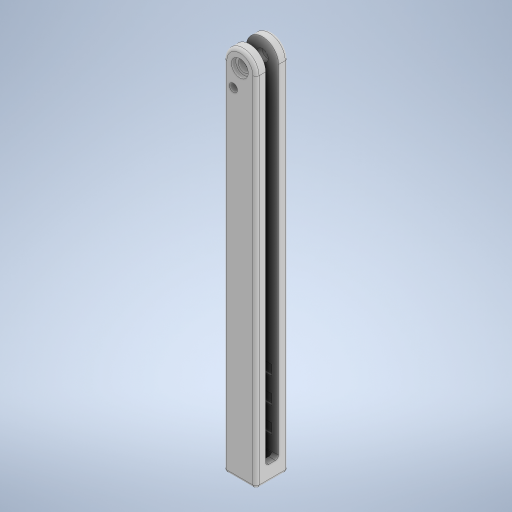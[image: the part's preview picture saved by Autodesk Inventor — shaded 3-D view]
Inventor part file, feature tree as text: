
AUTODESK INVENTOR PART (.ipt)
format: ipt  version: 2023.5 (Build 275446000, 446)  size: 356,352 bytes
history: native  units: mm
features: extrude x6, sketch x5, fillet x1, plane x1, mirror x1
ambient origin geometry x8: Origin, YZ Plane, XZ Plane, XY Plane, X Axis, Y Axis, Z Axis, Center Point
bodies: Solid1 (feature_tree)
feature tree (14):
  extrude  "Extrusion1"  Depth=12.7mm
  sketch  "Sketch2"  dims[d2=4.572mm d3=12.7mm d4=0.0mm]
  extrude  "Extrusion2"  Depth=12.7mm TaperAngle=0.0deg
  extrude  "Extrusion3"  Depth=5.08mm
  extrude  "Extrusion4"  Depth=120.048mm
  fillet  "Fillet1"  Radius=5.08mm
  extrude  "Extrusion6"  Depth=8.89mm TaperAngle=0.0deg
  plane  "Work Plane1"
  mirror  "Mirror1"
  extrude  "Extrusion7"  TaperAngle=0.0deg  [1 undecoded]
  sketch  "Sketch1"  dims[d0=12.7mm d1=140.97mm]
  sketch  "Sketch3"  dims[d5=6.35mm d6=5.08mm]
  sketch  "Sketch5"  dims[d7=3.81mm d8=120.048mm d9=5.08mm]
  sketch  "Sketch6"  dims[d10=24.0mm d11=8.89mm d12=0.0mm d13=0.0mm d14=0.0mm d15=3.175mm d16=7.954mm d17=2.54mm d18=0.0mm d19=0.0mm d20=1.2mm d25=6.604mm d26=1.651mm d27=0.0mm d29=10.0mm d31=40.0mm d32=7.0mm d33=4.0mm d34=10.0mm d35=10.0mm d36=2.0mm d37=1.5mm d38=10.0mm d39=0.0mm]
note: 1 required parameter value undecoded (feature->parameter linkage not recoverable at this tier; creation-order binding heuristic only, values carry confidence <= 0.55)
